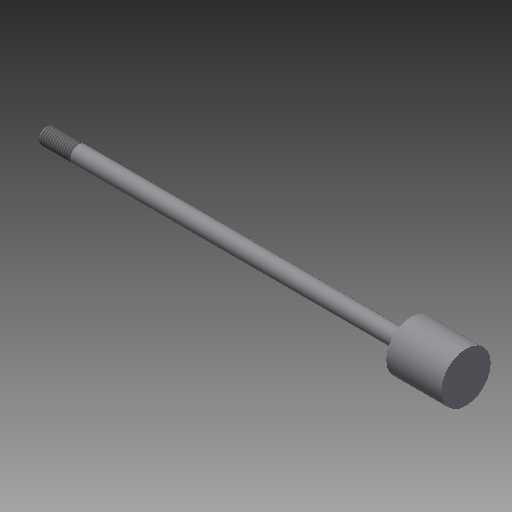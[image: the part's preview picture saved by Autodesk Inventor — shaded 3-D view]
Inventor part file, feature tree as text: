
AUTODESK INVENTOR PART (.ipt)
format: ipt  version: 2019 (Build 230136000, 136)  size: 153,600 bytes
history: native  units: in
note: dims shown in document units (in); Inventor stores cm internally (conversion verified against a paired STEP export)
features: other x84, revolve x3, sketch x3, thread x1
ambient origin geometry x8: Origin, YZ Plane, XZ Plane, XY Plane, X Axis, Y Axis, Z Axis, Center Point
bodies: Solid1 (feature_tree)
feature tree (91):
  revolve  "Revolution1"  Angle=360.0deg
  revolve  "Revolution2"  Angle=360.0deg
  thread  "Thread1"  [1 undecoded]
  revolve  "Revolution3"  [1 undecoded]
  other  "dia1_XY"
  other  "dia1_YZ"
  other  "dia1_ZX"
  other  "dia1_X"
  other  "dia1_Y"
  other  "dia1_Z"
  other  "dia1_Center"
  other  "dia12_XY"
  other  "dia12_YZ"
  other  "dia12_ZX"
  other  "dia12_X"
  other  "dia12_Y"
  other  "dia12_Z"
  other  "dia12_Center"
  other  "dia2_XY"
  other  "dia2_YZ"
  other  "dia2_ZX"
  other  "dia2_X"
  other  "dia2_Y"
  other  "dia2_Z"
  other  "dia2_Center"
  other  "dia22_XY"
  other  "dia22_YZ"
  other  "dia22_ZX"
  other  "dia22_X"
  other  "dia22_Y"
  other  "dia22_Z"
  other  "dia22_Center"
  other  "hh1_XY"
  other  "hh1_YZ"
  other  "hh1_ZX"
  other  "hh1_X"
  other  "hh1_Y"
  other  "hh1_Z"
  other  "hh1_Center"
  other  "hh2_XY"
  other  "hh2_YZ"
  other  "hh2_ZX"
  other  "hh2_X"
  other  "hh2_Y"
  other  "hh2_Z"
  other  "hh2_Center"
  other  "rl1_XY"
  other  "rl1_YZ"
  other  "rl1_ZX"
  other  "rl1_X"
  other  "rl1_Y"
  other  "rl1_Z"
  other  "rl1_Center"
  other  "rl2_XY"
  other  "rl2_YZ"
  other  "rl2_ZX"
  other  "rl2_X"
  other  "rl2_Y"
  other  "rl2_Z"
  other  "rl2_Center"
  other  "rod_cp_XY"
  other  "rod_cp_YZ"
  other  "rod_cp_ZX"
  other  "rod_cp_X"
  other  "rod_cp_Y"
  other  "rod_cp_Z"
  other  "rod_cp_Center"
  other  "thd1_XY"
  other  "thd1_YZ"
  other  "thd1_ZX"
  other  "thd1_X"
  other  "thd1_Y"
  other  "thd1_Z"
  other  "thd1_Center"
  other  "thd2_XY"
  other  "thd2_YZ"
  other  "thd2_ZX"
  other  "thd2_X"
  other  "thd2_Y"
  other  "thd2_Z"
  other  "thd2_Center"
  other  "to_rod_clevis_XY"
  other  "to_rod_clevis_YZ"
  other  "to_rod_clevis_ZX"
  other  "to_rod_clevis_X"
  other  "to_rod_clevis_Y"
  other  "to_rod_clevis_Z"
  other  "to_rod_clevis_Center"
  sketch  "Sketch_1"  dims[d0=360.0deg d1=360.0deg]
  sketch  "Sketch_3"  dims[d2=0.4787in d3=0.0in d4=360.0deg]
  sketch  "Sketch_30"  dims[d5=0.0in d6=0.0in d7=0.0in d8=0.0in d9=0.0in]
note: 2 required parameter values undecoded (feature->parameter linkage not recoverable at this tier; creation-order binding heuristic only, values carry confidence <= 0.55)
